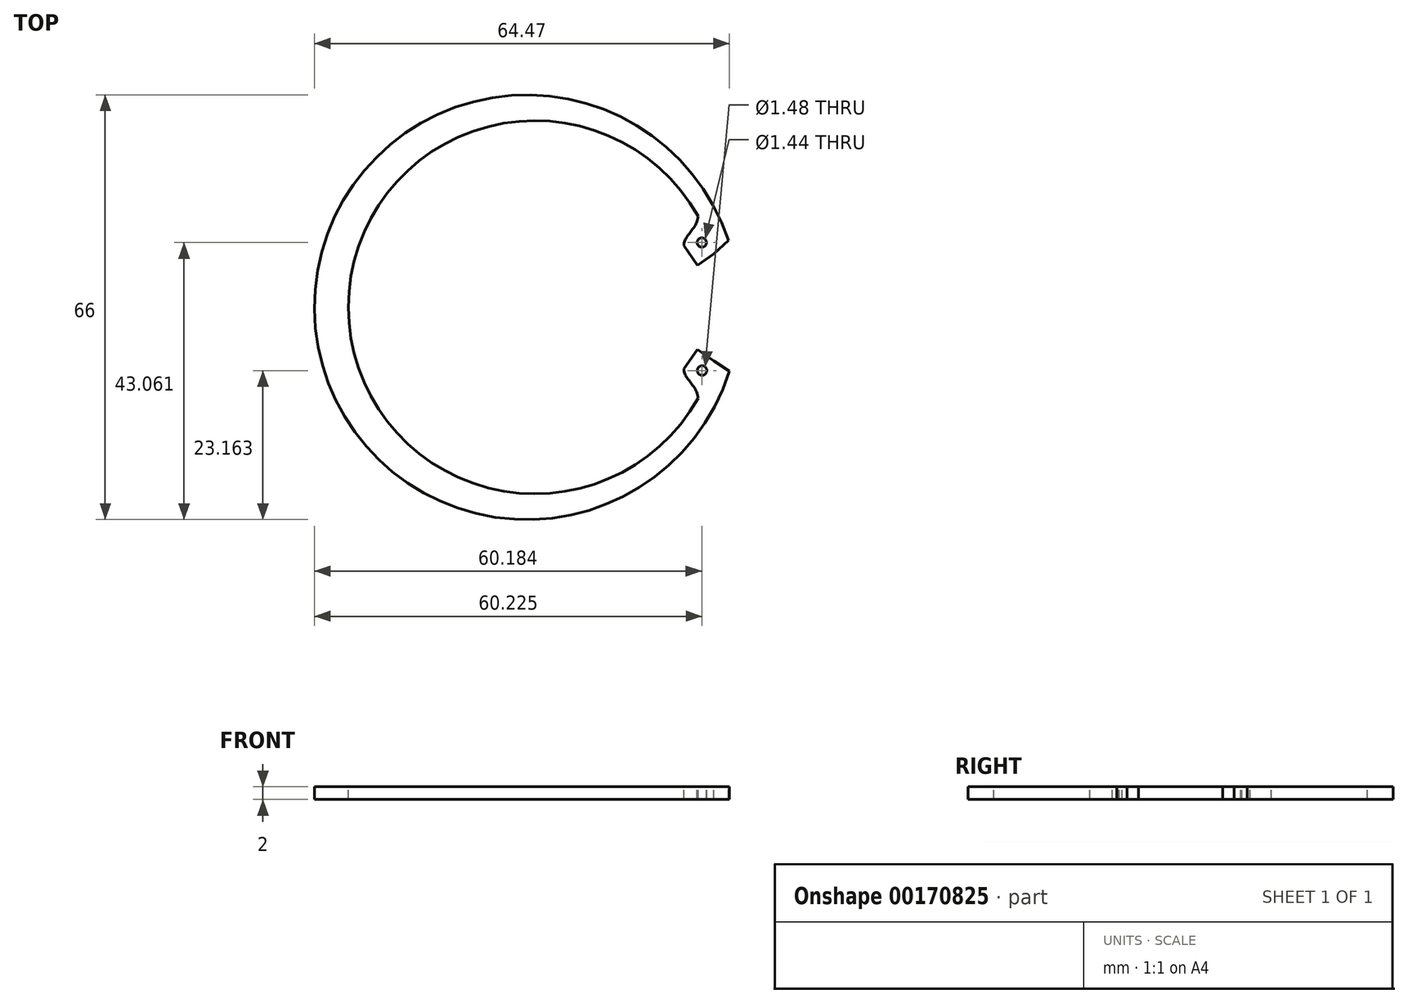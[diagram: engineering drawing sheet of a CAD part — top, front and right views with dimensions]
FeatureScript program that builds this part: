
annotation { "Feature Type Name" : "Feature", "Feature Type Description" : "" }
export const myFeature = defineFeature(function(context is Context, id is Id, definition is map)
    precondition{}
    {
        {
            var Q0;
            Q0=qCreatedBy(makeId("Top.planeOp"),FACE);
            var sketch = newSketch(context, id + "F0", { "sketchPlane" : qUnion([Q0])});
            skCircle(sketch, "E0", {"center": v(0, 0) * mm, "radius": 33 * mm});
            skSolve(sketch);
        }
        {
            var Q0;
            Q0 = qSketchRegion(id + "F0", true);
            extrude(context, id + "F1", {"entities" : qUnion([Q0]), "depth" : 2 * mm});
        }
        {
            var Q0;
            Q0=makeQuery(id+"F1.opExtrude","CAP_FACE",FACE,{"disambiguationData":[OSD([sQuery(id+"F0.wireOp",EDGE,"E0")])],"isStart":false});
            var sketch = newSketch(context, id + "F2", { "sketchPlane" : qUnion([Q0])});
            skCircle(sketch, "E1", {"center": v(1.28, 0) * mm, "radius": 29 * mm});
            skLineSegment(sketch, "E2", {"start": v(31.45, 10) * mm, "end": v(26.54, 6.54) * mm});
            skLineSegment(sketch, "E3", {"start": v(26.54, 6.54) * mm, "end": v(24.42, 9.55) * mm});
            skFitSpline(sketch, "E4", {"points": [v(24.42, 9.55) * mm, v(26.62, 14.1) * mm, v(17.68, 23.92) * mm], "startDerivative": vector(-0.97, 11.97) * mm, "endDerivative": vector(-19.05, 6.4) * mm});
            skLineSegment(sketch, "E5", {"start": v(0, 0) * mm, "end": v(65.06, 0) * mm});
            skLineSegment(sketch, "E6.MirrorCS", {"start": v(26.54, -6.54) * mm, "end": v(24.42, -9.55) * mm});
            skLineSegment(sketch, "E7.MirrorCS", {"start": v(31.45, -10) * mm, "end": v(26.54, -6.54) * mm});
            skFitSpline(sketch, "E8.MirrorCS", {"points": [v(24.42, -9.55) * mm, v(26.62, -14.1) * mm, v(17.68, -23.92) * mm], "startDerivative": vector(-0.97, -11.97) * mm, "endDerivative": vector(-19.05, -6.4) * mm});
            skSolve(sketch);
        }
        {
            var Q0;
            {var subQ4=sQuery(id+"F2.wireOp",EDGE,"E3");Q0=makeQuery(id+"F2.imprint","IMPRINT",FACE,{"disambiguationData":[TD([[makeQuery(id+"F2.imprint","IMPRINT",EDGE,{"derivedFrom":subQ4}),1.0]])]});}
            extrude(context, id + "F3", {"entities" : qUnion([Q0]), "operationType" : NewBodyOperationType.REMOVE, "endBound" : BoundingType.THROUGH_ALL, "oppositeDirection" : true, "depth" : 25 * mm});
        }
        {
            var Q0;
            Q0=makeQuery(id+"F1.opExtrude","CAP_FACE",FACE,{"disambiguationData":[OSD([sQuery(id+"F0.wireOp",EDGE,"E0")])],"isStart":false});
            var sketch = newSketch(context, id + "F4", { "sketchPlane" : qUnion([Q0])});
            skLineSegment(sketch, "E9", {"start": v(29.06, 8.32) * mm, "end": v(31.33, 10.36) * mm});
            skLineSegment(sketch, "E10", {"start": v(29.06, 8.32) * mm, "end": v(29.06, -8.32) * mm});
            skLineSegment(sketch, "E11", {"start": v(29.06, -8.32) * mm, "end": v(31.47, -9.93) * mm});
            skLineSegment(sketch, "E12", {"start": v(31.47, -9.93) * mm, "end": v(41.95, 0) * mm});
            skLineSegment(sketch, "E13", {"start": v(41.95, 0) * mm, "end": v(31.33, 10.36) * mm});
            skSolve(sketch);
        }
        {
            var Q0;
            Q0 = qSketchRegion(id + "F4", true);
            extrude(context, id + "F5", {"entities" : qUnion([Q0]), "operationType" : NewBodyOperationType.REMOVE, "endBound" : BoundingType.THROUGH_ALL, "oppositeDirection" : true, "depth" : 25 * mm});
        }
        {
            var Q0;
            Q0=makeQuery(id+"F1.opExtrude","CAP_FACE",FACE,{"disambiguationData":[OSD([sQuery(id+"F0.wireOp",EDGE,"E0")])],"isStart":false});
            var sketch = newSketch(context, id + "F6", { "sketchPlane" : qUnion([Q0])});
            skCircle(sketch, "E14", {"center": v(27.18, 10.06) * mm, "radius": 0.72 * mm});
            skCircle(sketch, "E15", {"center": v(27.23, -9.84) * mm, "radius": 0.74 * mm});
            skSolve(sketch);
        }
        {
            var Q0;
            Q0 = qSketchRegion(id + "F6", true);
            extrude(context, id + "F7", {"entities" : qUnion([Q0]), "operationType" : NewBodyOperationType.REMOVE, "endBound" : BoundingType.THROUGH_ALL, "oppositeDirection" : true, "depth" : 25 * mm});
        }
    });
